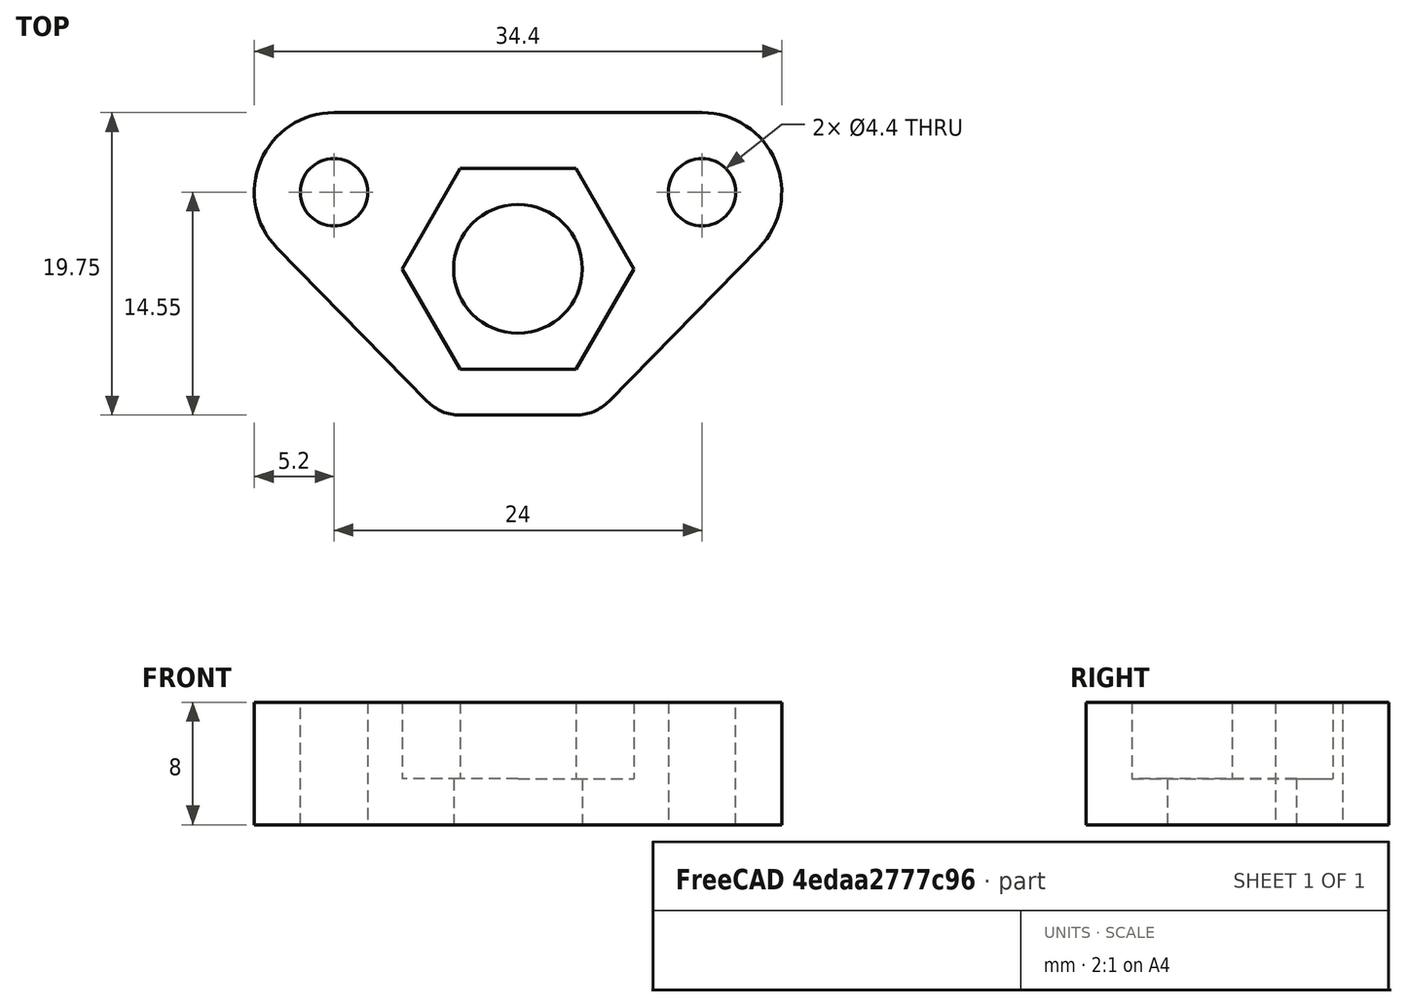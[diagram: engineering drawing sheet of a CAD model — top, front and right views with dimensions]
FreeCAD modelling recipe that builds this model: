
FCSTD DOCUMENT  (FreeCAD 0.18.4R)
Label: 18
License: All rights reserved
LicenseURL: http://en.wikipedia.org/wiki/All_rights_reserved
objects: Sketcher::SketchObject×2, PartDesign::Pad×1, PartDesign::Pocket×1, PartDesign::Mirrored×1, PartDesign::Body×1
note: 8 computed .brp shape members not serialized (recipe doc carries the construction recipe); baked Part::Feature solids carry a one-line shape summary decoded from their .brp

FEATURE [Sketcher::SketchObject] Sketch
  MapMode = 5
  Support = -> [XY_Plane]
  constraints (43):
    c: PointOnObject(g0,g-2)
    c: PointOnObject(g0,g-2)
    c: Coincident(g0,g-1)
    c: Diameter(g1) = 4.4
    c: Distance(g1,g-2) = 12
    c: Diameter(g0) = 8.4
    c: Distance(g1,g-1) = 5
    c: PointOnObject(g2,g-2)
    c: Horizontal(g2)
    c: PointOnObject(g3,g-2)
    c: Horizontal(g3)
    c: Coincident(g4,g1)
    c: Coincident(g4,g2)
    c: Coincident(g5,g4)
    c: Coincident(g6,g0)
    c: Coincident(g6,g2)
    c: Coincident(g7,g0)
    c: Coincident(g7,g3)
    c: Coincident(g8,g9)
    c: Coincident(g9,g10)
    c: Coincident(g10,g11)
    c: Coincident(g11,g12)
    c: Coincident(g12,g13)
    c: Coincident(g13,g8)
    c: Equal(g8, g9-g13) x5
    c: PointOnObject(g8,g14)
    c: PointOnObject(g9,g14)
    c: PointOnObject(g10,g14)
    c: PointOnObject(g11,g14)
    c: PointOnObject(g12,g14)
    c: PointOnObject(g13,g14)
    c: Coincident(g14,g0)
    c: Horizontal(g11)
    c: Distance(g11,g8) = 13.1
    c: Coincident(g15,g11)
    c: Coincident(g15,g5)
    c: Coincident(g15,g3)
    c: Tangent(g3,g15)
    c: Tangent(g15,g5)
    c: Tangent(g5,g4)
    c: Tangent(g2,g4)
    c: Diameter(g15) = 6
    c: Radius(g4) = 5.2
FEATURE [PartDesign::Pad] Pad
  Length = 8
  Length2 = 100
  Profile = -> Sketch
  Type = 0
FEATURE [Sketcher::SketchObject] Sketch001  label="Unnamed"
  constraints (16):
    c: Coincident(g0,g1)
    c: Coincident(g1,g2)
    c: Coincident(g2,g3)
    c: Coincident(g3,g4)
    c: Coincident(g4,g5)
    c: Coincident(g5,g0)
    c: Equal(g0, g1-g5) x5
    c: PointOnObject(g0,g6)
    c: PointOnObject(g1,g6)
    c: PointOnObject(g2,g6)
    c: PointOnObject(g3,g6)
    c: PointOnObject(g4,g6)
    c: PointOnObject(g5,g6)
    c: Coincident(g6,g-1)
    c: Horizontal(g3)
    c: Distance(g0,g2) = 13.1
FEATURE [PartDesign::Pocket] Pocket  label="Unnamed"
  Length = 100
  Length2 = 100
  Type = 0
FEATURE [PartDesign::Mirrored] Mirrored  label="Unnamed"
FEATURE [PartDesign::Body] Body
  Group = -> [Sketch,Pad,Sketch001,Pocket,Mirrored]
  Origin = -> Origin
  Tip = -> Mirrored
